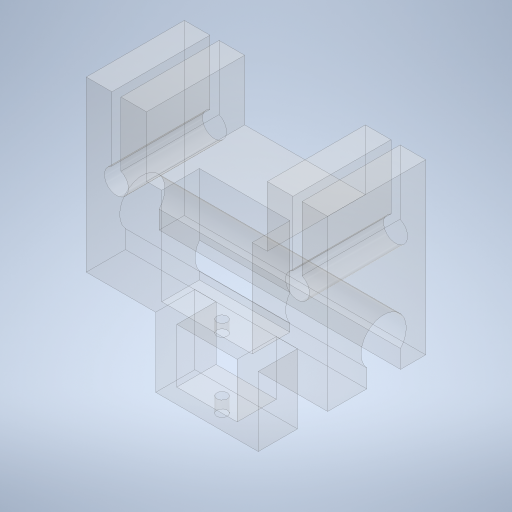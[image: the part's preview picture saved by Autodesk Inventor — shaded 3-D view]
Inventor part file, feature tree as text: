
AUTODESK INVENTOR PART (.ipt)
format: ipt  version: 2023 (Build 270158000, 158)  size: 479,232 bytes
history: native  units: mm
features: extrude x11, sketch x11, projected_geometry x5
ambient origin geometry x8: Origin, YZ Plane, XZ Plane, XY Plane, X Axis, Y Axis, Z Axis, Center Point
bodies: Solid1 (feature_tree)
feature tree (27):
  extrude  "Extrusion1"  Depth=10.0mm
  extrude  "Extrusion5"  Depth=1.5mm
  extrude  "Extrusion11"  Depth=10.0mm
  extrude  "Extrusion13"  Depth=80.0mm
  extrude  "Extrusion14"  TaperAngle=0.0deg  [1 undecoded]
  extrude  "Extrusion15"  Depth=20.0mm
  extrude  "Extrusion16"  Depth=20.0mm
  extrude  "Extrusion17"  Depth=10.0mm
  extrude  "Extrusion18"  Depth=20.0mm
  extrude  "Extrusion19"  Depth=35.0mm
  extrude  "Extrusion20"  Depth=80.0mm TaperAngle=0.0deg
  sketch  "Sketch1"  dims[d2=8.0mm d3=10.0mm]
  sketch  "Sketch5"  dims[d7=1.5mm d8=1.5mm]
  sketch  "Sketch13"  dims[d9=36.0mm d10=0.0mm d16=10.0mm]
  projected_geometry  "Projected Loop1"
  sketch  "Sketch16"  dims[d17=8.0mm d18=1.5mm d19=1.5mm d20=10.0mm d21=8.0mm d22=80.0mm]
  sketch  "Sketch17"  dims[d23=10.0mm d24=0.0mm]
  sketch  "Sketch18"  dims[d25=60.0mm d26=20.0mm]
  sketch  "Sketch19"  dims[d27=20.0mm d28=20.0mm]
  sketch  "Sketch20"  dims[d29=20.0mm d30=10.0mm]
  sketch  "Sketch21"  dims[d31=10.0mm d32=20.0mm]
  projected_geometry  "Projected Loop2"
  sketch  "Sketch22"  dims[d40=30.0mm d41=35.0mm]
  projected_geometry  "Projected Loop3"
  projected_geometry  "Projected Loop4"
  projected_geometry  "Projected Loop5"
  sketch  "Sketch23"  dims[d45=20.0mm d46=80.0mm d47=0.0mm d79=25.0mm d82=25.0mm d83=1.0mm d84=0.0mm d85=15.0mm d86=5.0mm d87=15.0mm d103=6.0mm d104=0.0mm d105=20.0mm d106=0.0mm d107=30.0mm d108=25.0mm d109=15.0mm d110=0.0mm d111=37.0mm d112=0.0mm d113=7.0mm d114=7.0mm d115=5.0mm d116=18.0mm d117=20.0mm d118=23.0mm d119=15.5mm d120=0.0mm d121=3.5mm d122=7.5mm d123=40.0mm d124=80.0mm d125=0.0mm d126=2.5mm d127=0.0mm d128=15.0mm d129=0.0mm d130=20.0mm d131=20.0mm d132=20.0mm d133=0.0mm]
note: 1 required parameter value undecoded (feature->parameter linkage not recoverable at this tier; creation-order binding heuristic only, values carry confidence <= 0.55)
